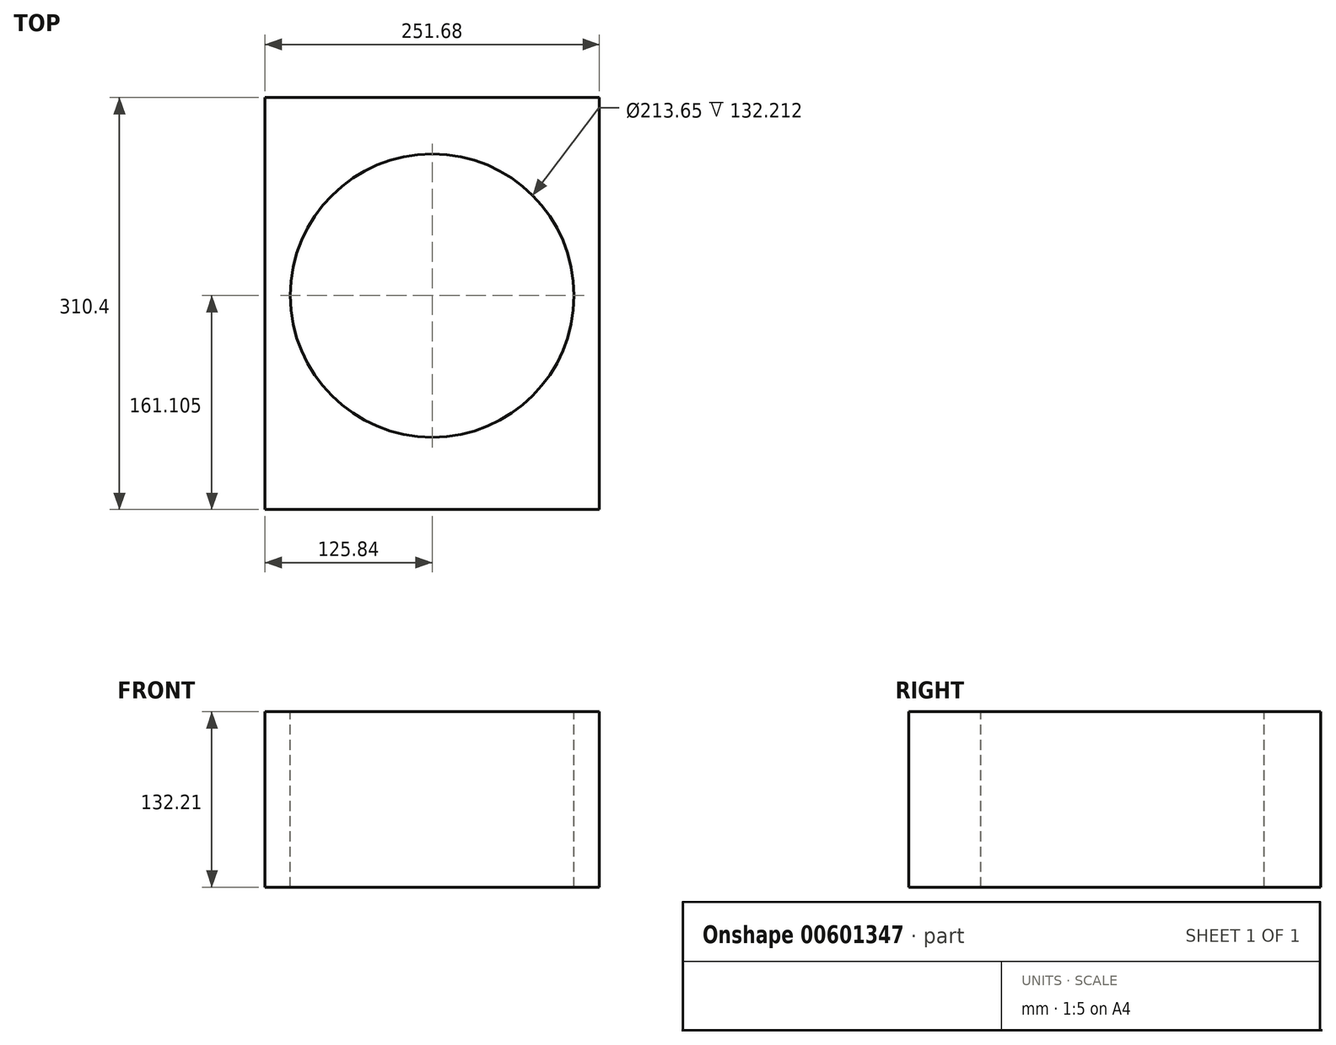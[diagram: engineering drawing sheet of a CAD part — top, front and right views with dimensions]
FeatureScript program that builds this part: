
annotation { "Feature Type Name" : "Feature", "Feature Type Description" : "" }
export const myFeature = defineFeature(function(context is Context, id is Id, definition is map)
    precondition{}
    {
        {
            var Q0;
            Q0=qCreatedBy(makeId("Top.planeOp"),FACE);
            var sketch = newSketch(context, id + "F0", { "sketchPlane" : qUnion([Q0])});
            skLineSegment(sketch, "E0.bottom", {"start": v(125.84, -127.53) * mm, "end": v(-125.84, -127.53) * mm});
            skLineSegment(sketch, "E0.top", {"start": v(125.84, 182.87) * mm, "end": v(-125.84, 182.87) * mm});
            skLineSegment(sketch, "E0.left", {"start": v(125.84, -127.53) * mm, "end": v(125.84, 182.87) * mm});
            skLineSegment(sketch, "E0.right", {"start": v(-125.84, -127.53) * mm, "end": v(-125.84, 182.87) * mm});
            skPoint(sketch, "E0.middle", {"position": v(0, 27.67) * mm});
            skSolve(sketch);
        }
        {
            var Q0;
            Q0=makeQuery(id+"F0.imprint","IMPRINT",FACE,{"disambiguationData":[TD([[makeQuery(id+"F0.imprint","IMPRINT",EDGE,{"derivedFrom":sQuery(id+"F0.wireOp",EDGE,"E0.bottom")}),-1.0]])]});
            var sketch = newSketch(context, id + "F1", { "sketchPlane" : qUnion([Q0])});
            skSolve(sketch);
        }
        {
            var Q0;
            Q0 = qSketchRegion(id + "F1", true);
            var Q1;
            Q1=makeQuery(id+"F0.imprint","IMPRINT",FACE,{"disambiguationData":[TD([[makeQuery(id+"F0.imprint","IMPRINT",EDGE,{"derivedFrom":sQuery(id+"F0.wireOp",EDGE,"E0.bottom")}),-1.0]])]});
            extrude(context, id + "F2", {"entities" : qUnion([Q0, Q1]), "depth" : 132.21 * mm, "offsetDistance" : 25.4 * mm});
        }
        {
            var Q0;
            Q0=makeQuery(id+"F2.opExtrude","CAP_FACE",FACE,{"disambiguationData":[OSD([sQuery(id+"F0.wireOp",EDGE,"E0.bottom"),sQuery(id+"F0.wireOp",EDGE,"E0.top"),sQuery(id+"F0.wireOp",EDGE,"E0.left"),sQuery(id+"F0.wireOp",EDGE,"E0.right")])],"isStart":false});
            var sketch = newSketch(context, id + "F3", { "sketchPlane" : qUnion([Q0])});
            skCircle(sketch, "E1", {"center": v(0, 33.58) * mm, "radius": 106.82 * mm});
            skSolve(sketch);
        }
        {
            var Q0;
            Q0 = qSketchRegion(id + "F3", true);
            var Q1;
            Q1=makeQuery(id+"F3.imprint","IMPRINT",FACE,{"disambiguationData":[TD([[makeQuery(id+"F3.imprint","IMPRINT",EDGE,{"derivedFrom":sQuery(id+"F3.wireOp",EDGE,"E1")}),1.0]])]});
            extrude(context, id + "F4", {"entities" : qUnion([Q0, Q1]), "operationType" : NewBodyOperationType.REMOVE, "oppositeDirection" : true, "depth" : 281.75 * mm, "offsetDistance" : 25.4 * mm});
        }
    });
